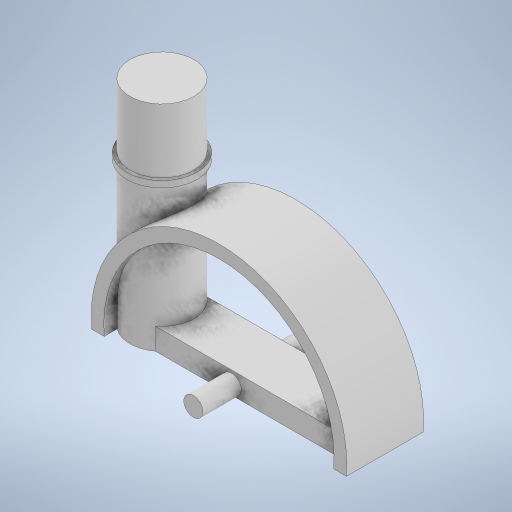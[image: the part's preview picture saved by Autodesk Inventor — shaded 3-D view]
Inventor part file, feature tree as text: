
AUTODESK INVENTOR PART (.ipt)
format: ipt  version: 2023 (Build 270158030, 158C)  size: 320,000 bytes
history: native  units: in
note: dims shown in document units (in); Inventor stores cm internally (conversion verified against a paired STEP export)
features: extrude x6, sketch x6
ambient origin geometry x8: Origin, YZ Plane, XZ Plane, XY Plane, X Axis, Y Axis, Z Axis, Center Point
bodies: Solid1 (feature_tree)
feature tree (12):
  extrude  "Extrusion1"  Depth=0.5in TaperAngle=0.0deg
  extrude  "Extrusion2"  Depth=0.05in TaperAngle=0.0deg
  extrude  "Extrusion3"  Depth=0.5in TaperAngle=0.0deg
  extrude  "Extrusion4"  Depth=1.05in
  extrude  "Extrusion5"  Depth=0.9955in
  extrude  "Extrusion6"  Depth=0.1in
  sketch  "Sketch1"  dims[d0=0.5in d1=0.5in d2=0.0in]
  sketch  "Sketch2"  dims[d3=0.55in d4=0.05in d5=0.0in]
  sketch  "Sketch3"  dims[d6=0.5in d7=1.125in d8=0.0in]
  sketch  "Sketch4"  dims[d11=1.8in d12=1.05in]
  sketch  "Sketch5"  dims[d13=2.0in d14=0.9955in]
  sketch  "Sketch6"  dims[d15=0.6in d16=0.0in d17=0.1in d18=0.1in d21=0.1698in d22=0.0002in d23=0.0002in d24=1.975in d25=0.0in d26=0.15in d27=1.0in d28=0.0in d10=0.5in]
